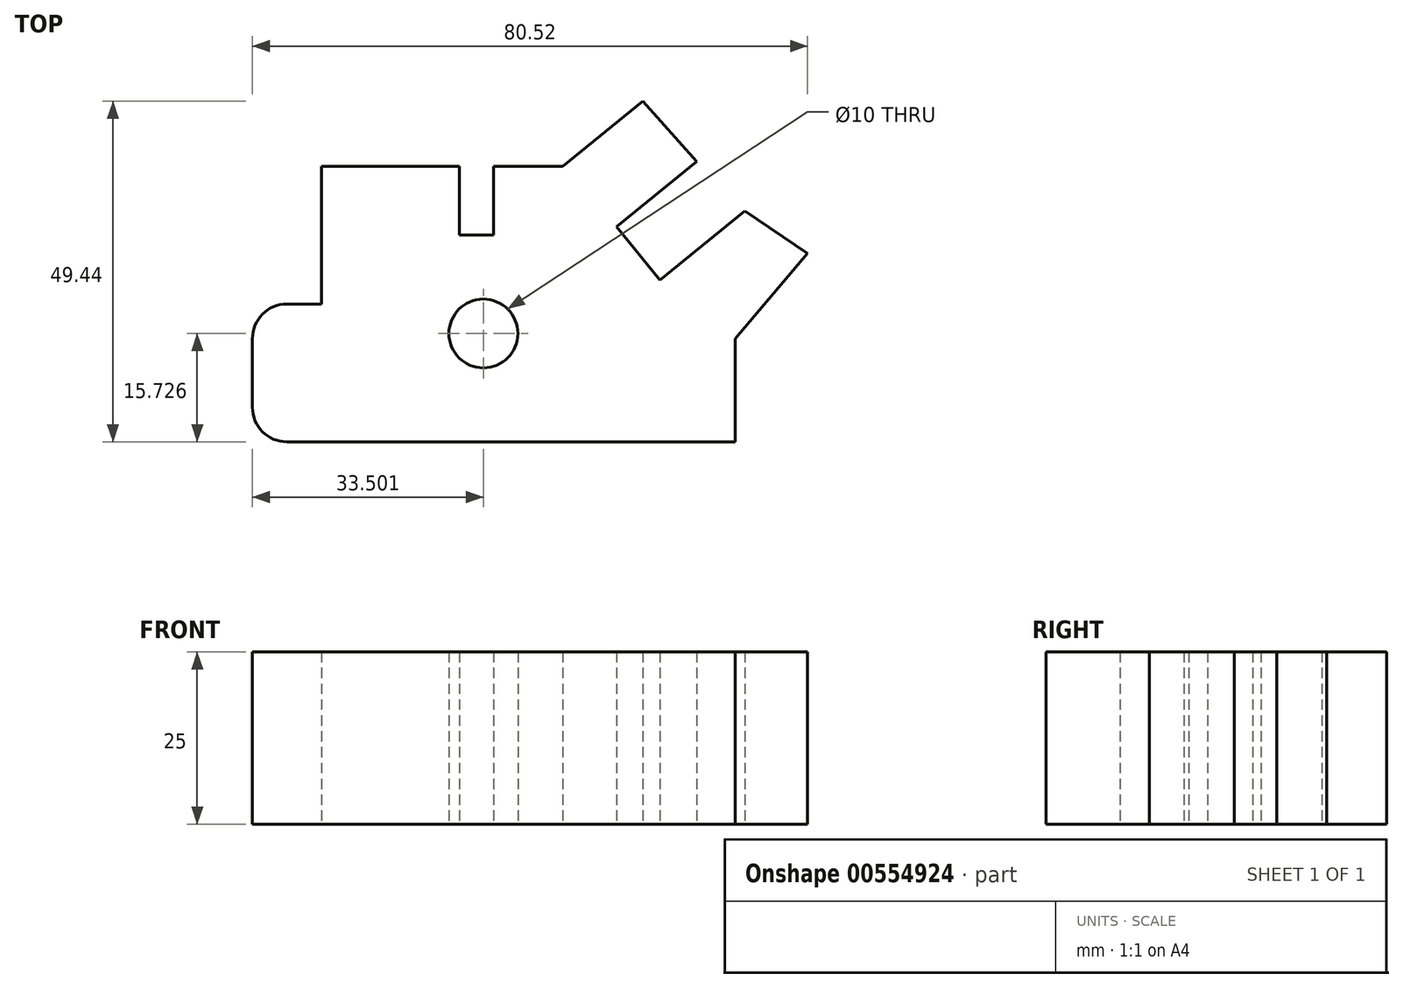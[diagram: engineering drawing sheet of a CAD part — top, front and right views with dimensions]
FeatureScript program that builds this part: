
annotation { "Feature Type Name" : "Feature", "Feature Type Description" : "" }
export const myFeature = defineFeature(function(context is Context, id is Id, definition is map)
    precondition{}
    {
        {
            var Q0;
            Q0=qCreatedBy(makeId("Top.planeOp"),FACE);
            var sketch = newSketch(context, id + "F0", { "sketchPlane" : qUnion([Q0])});
            skLineSegment(sketch, "E0", {"start": v(27.73, -27.34) * mm, "end": v(-37.27, -27.34) * mm});
            skLineSegment(sketch, "E1", {"start": v(-42.27, -22.34) * mm, "end": v(-42.27, -12.34) * mm});
            skLineSegment(sketch, "E2", {"start": v(-37.27, -7.34) * mm, "end": v(-32.27, -7.34) * mm});
            skLineSegment(sketch, "E3", {"start": v(-32.27, -7.34) * mm, "end": v(-32.27, 12.66) * mm});
            skLineSegment(sketch, "E4", {"start": v(-32.27, 12.66) * mm, "end": v(-12.27, 12.66) * mm});
            skLineSegment(sketch, "E5", {"start": v(-12.27, 12.66) * mm, "end": v(-12.27, 2.66) * mm});
            skLineSegment(sketch, "E6", {"start": v(-12.27, 2.66) * mm, "end": v(-7.27, 2.66) * mm});
            skLineSegment(sketch, "E7", {"start": v(-7.27, 2.66) * mm, "end": v(-7.27, 12.66) * mm});
            skLineSegment(sketch, "E8", {"start": v(27.73, -27.34) * mm, "end": v(27.73, -12.34) * mm});
            skLineSegment(sketch, "E9", {"start": v(-7.27, 12.66) * mm, "end": v(2.73, 12.66) * mm});
            skLineSegment(sketch, "E10", {"start": v(10.51, 3.88) * mm, "end": v(16.83, -3.88) * mm});
            skLineSegment(sketch, "E11", {"start": v(2.73, 12.66) * mm, "end": v(14.38, 22.1) * mm});
            skLineSegment(sketch, "E12", {"start": v(10.51, 3.88) * mm, "end": v(22.14, 13.35) * mm});
            skLineSegment(sketch, "E13", {"start": v(14.38, 22.1) * mm, "end": v(22.14, 13.35) * mm});
            skPoint(sketch, "E14.startSnap0", {"position": v(13.67, 0) * mm});
            skPoint(sketch, "E14.start.orphan", {"position": v(10.51, 0) * mm});
            skLineSegment(sketch, "E15", {"start": v(16.83, -3.88) * mm, "end": v(29.13, 6.15) * mm});
            skLineSegment(sketch, "E16", {"start": v(29.13, 6.15) * mm, "end": v(38.25, 0) * mm});
            skLineSegment(sketch, "E17", {"start": v(27.73, -12.34) * mm, "end": v(38.25, 0) * mm});
            skPoint(sketch, "E18.visualSharp", {"position": v(-42.27, -7.34) * mm});
            skArc(sketch, "E18.filletArc", {"start": v(-37.27, -7.34) * mm, "mid": v(-40.8, -8.8) * mm, "end": v(-42.27, -12.34) * mm});
            skPoint(sketch, "E19.visualSharp", {"position": v(-42.27, -27.34) * mm});
            skArc(sketch, "E19.filletArc", {"start": v(-42.27, -22.34) * mm, "mid": v(-40.8, -25.88) * mm, "end": v(-37.27, -27.34) * mm});
            skCircle(sketch, "E20", {"center": v(-8.77, -11.61) * mm, "radius": 5 * mm});
            skSolve(sketch);
        }
        {
            var Q0;
            Q0 = qSketchRegion(id + "F0", true);
            extrude(context, id + "F1", {"entities" : qUnion([Q0]), "depth" : 25 * mm, "offsetDistance" : 25 * mm});
        }
        {
            var Q0;
            Q0 = qSketchRegion(id + "F0", true);
            extrude(context, id + "F2", {"entities" : qUnion([Q0]), "operationType" : NewBodyOperationType.ADD, "depth" : 25 * mm, "offsetDistance" : 25 * mm});
        }
    });
